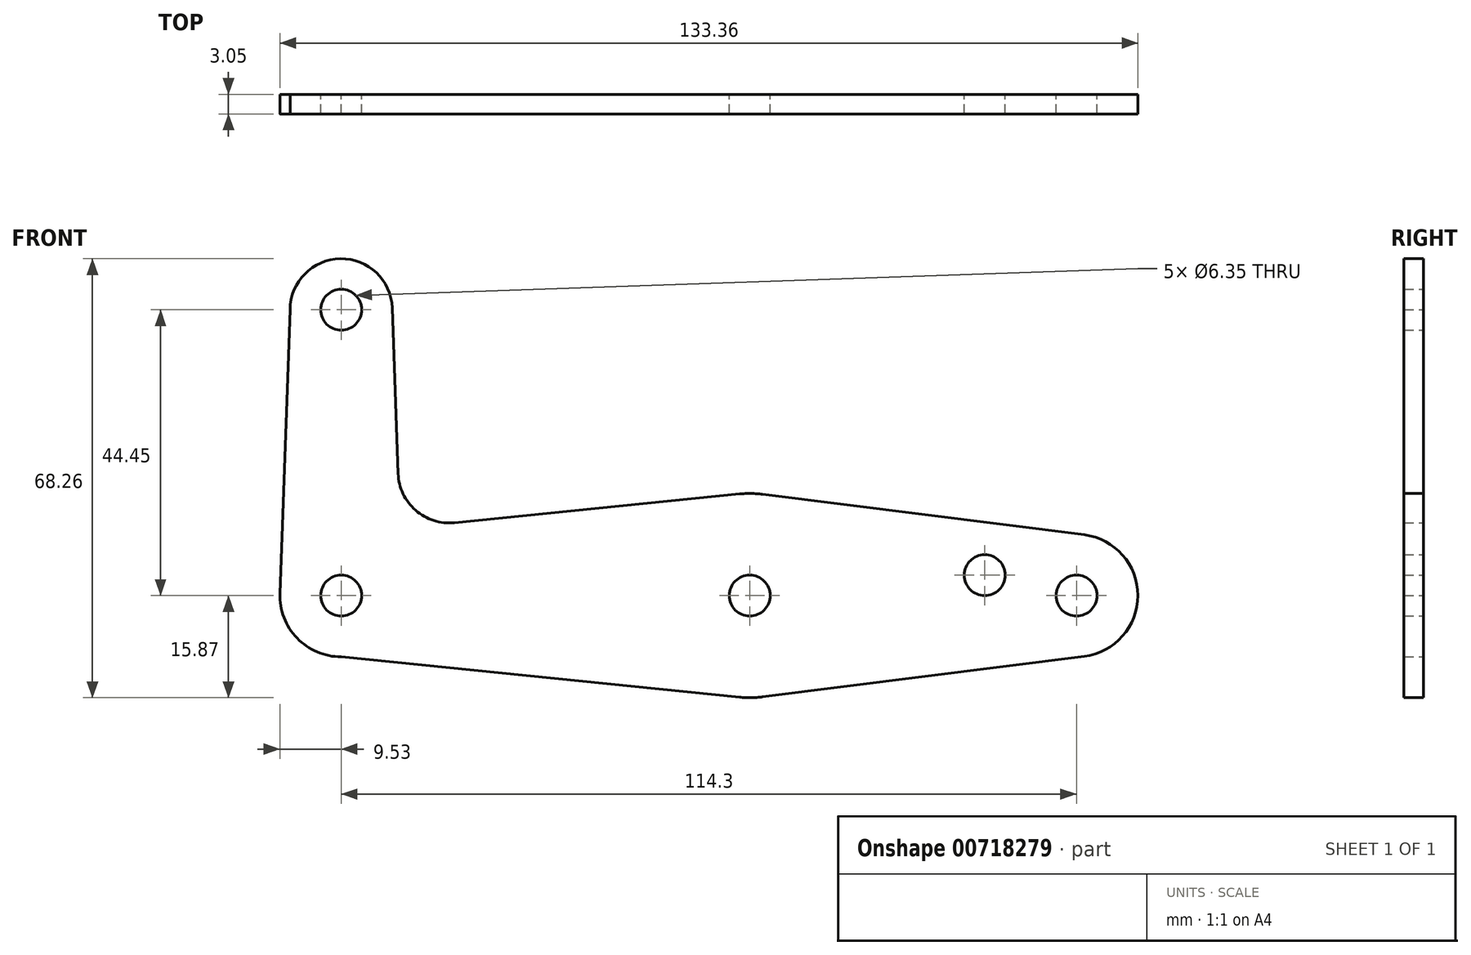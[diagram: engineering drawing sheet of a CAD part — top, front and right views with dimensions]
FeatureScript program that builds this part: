
annotation { "Feature Type Name" : "Feature", "Feature Type Description" : "" }
export const myFeature = defineFeature(function(context is Context, id is Id, definition is map)
    precondition{}
    {
        {
            var Q0;
            Q0=qCreatedBy(makeId("Front.planeOp"),FACE);
            var sketch = newSketch(context, id + "F0", { "sketchPlane" : qUnion([Q0])});
            skLineSegment(sketch, "E0", {"start": v(0, 0) * mm, "end": v(114.3, 0) * mm, "construction": true});
            skLineSegment(sketch, "E1", {"start": v(0, 0) * mm, "end": v(0, 44.45) * mm, "construction": true});
            skLineSegment(sketch, "E2", {"start": v(0, 0) * mm, "end": v(63.5, 0) * mm});
            skCircle(sketch, "E3", {"center": v(114.3, 0) * mm, "radius": 9.53 * mm});
            skCircle(sketch, "E4", {"center": v(63.5, 0) * mm, "radius": 15.88 * mm});
            skCircle(sketch, "E5", {"center": v(0, 44.45) * mm, "radius": 7.94 * mm});
            skCircle(sketch, "E6", {"center": v(0, 0) * mm, "radius": 9.53 * mm});
            skLineSegment(sketch, "E7", {"start": v(-7.94, 44.45) * mm, "end": v(-9.53, 0) * mm});
            skLineSegment(sketch, "E8", {"start": v(0, -9.53) * mm, "end": v(61.9, -15.8) * mm});
            skCircle(sketch, "E9", {"center": v(114.3, 0) * mm, "radius": 3.18 * mm});
            skCircle(sketch, "E10", {"center": v(100.03, 3.18) * mm, "radius": 3.18 * mm});
            skCircle(sketch, "E11", {"center": v(63.5, 0) * mm, "radius": 3.18 * mm});
            skCircle(sketch, "E12", {"center": v(0, 44.45) * mm, "radius": 3.18 * mm});
            skCircle(sketch, "E13", {"center": v(0, 0) * mm, "radius": 3.18 * mm});
            skLineSegment(sketch, "E14", {"start": v(65.48, 15.75) * mm, "end": v(115.5, 9.45) * mm});
            skLineSegment(sketch, "E15", {"start": v(7.93, 44.73) * mm, "end": v(8.85, 18.97) * mm});
            skLineSegment(sketch, "E16", {"start": v(17.6, 11.34) * mm, "end": v(61.91, 15.8) * mm});
            skArc(sketch, "E17.filletArc", {"start": v(8.85, 18.97) * mm, "mid": v(11.57, 13.26) * mm, "end": v(17.6, 11.34) * mm});
            skLineSegment(sketch, "E18", {"start": v(65.48, -15.75) * mm, "end": v(115.5, -9.45) * mm});
            skSolve(sketch);
        }
        {
            var Q0;
            Q0 = qSketchRegion(id + "F0", true);
            extrude(context, id + "F1", {"entities" : qUnion([Q0]), "depth" : 3.05 * mm, "offsetDistance" : 25.4 * mm});
        }
    });
